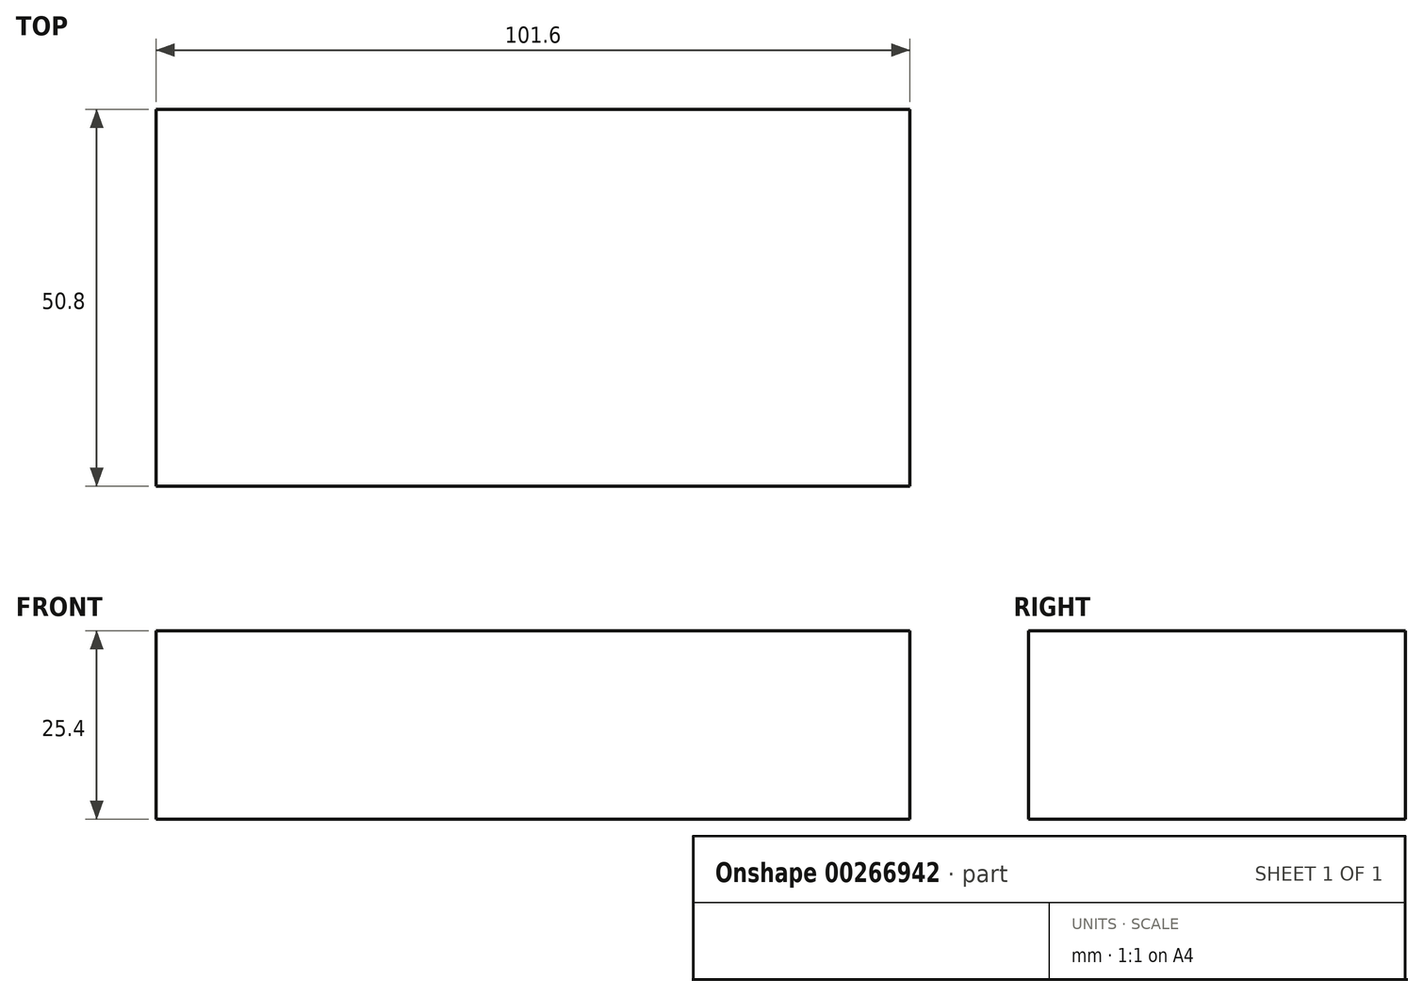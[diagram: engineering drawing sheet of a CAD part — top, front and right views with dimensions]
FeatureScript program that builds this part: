
annotation { "Feature Type Name" : "Feature", "Feature Type Description" : "" }
export const myFeature = defineFeature(function(context is Context, id is Id, definition is map)
    precondition{}
    {
        {
            var Q0;
            Q0=qCreatedBy(makeId("Top.planeOp"),FACE);
            var sketch = newSketch(context, id + "F0", { "sketchPlane" : qUnion([Q0])});
            skLineSegment(sketch, "E0.bottom", {"start": v(-46.96, 11.69) * mm, "end": v(54.64, 11.69) * mm});
            skLineSegment(sketch, "E0.top", {"start": v(-46.96, -39.11) * mm, "end": v(54.64, -39.11) * mm});
            skLineSegment(sketch, "E0.left", {"start": v(-46.96, 11.69) * mm, "end": v(-46.96, -39.11) * mm});
            skLineSegment(sketch, "E0.right", {"start": v(54.64, 11.69) * mm, "end": v(54.64, -39.11) * mm});
            skSolve(sketch);
        }
        {
            var Q0;
            Q0=makeQuery(id+"F0.imprint","IMPRINT",FACE,{"disambiguationData":[TD([[makeQuery(id+"F0.imprint","IMPRINT",EDGE,{"derivedFrom":sQuery(id+"F0.wireOp",EDGE,"E0.bottom")}),-1.0]])]});
            extrude(context, id + "F1", {"entities" : qUnion([Q0]), "depth" : 25.4 * mm});
        }
    });
